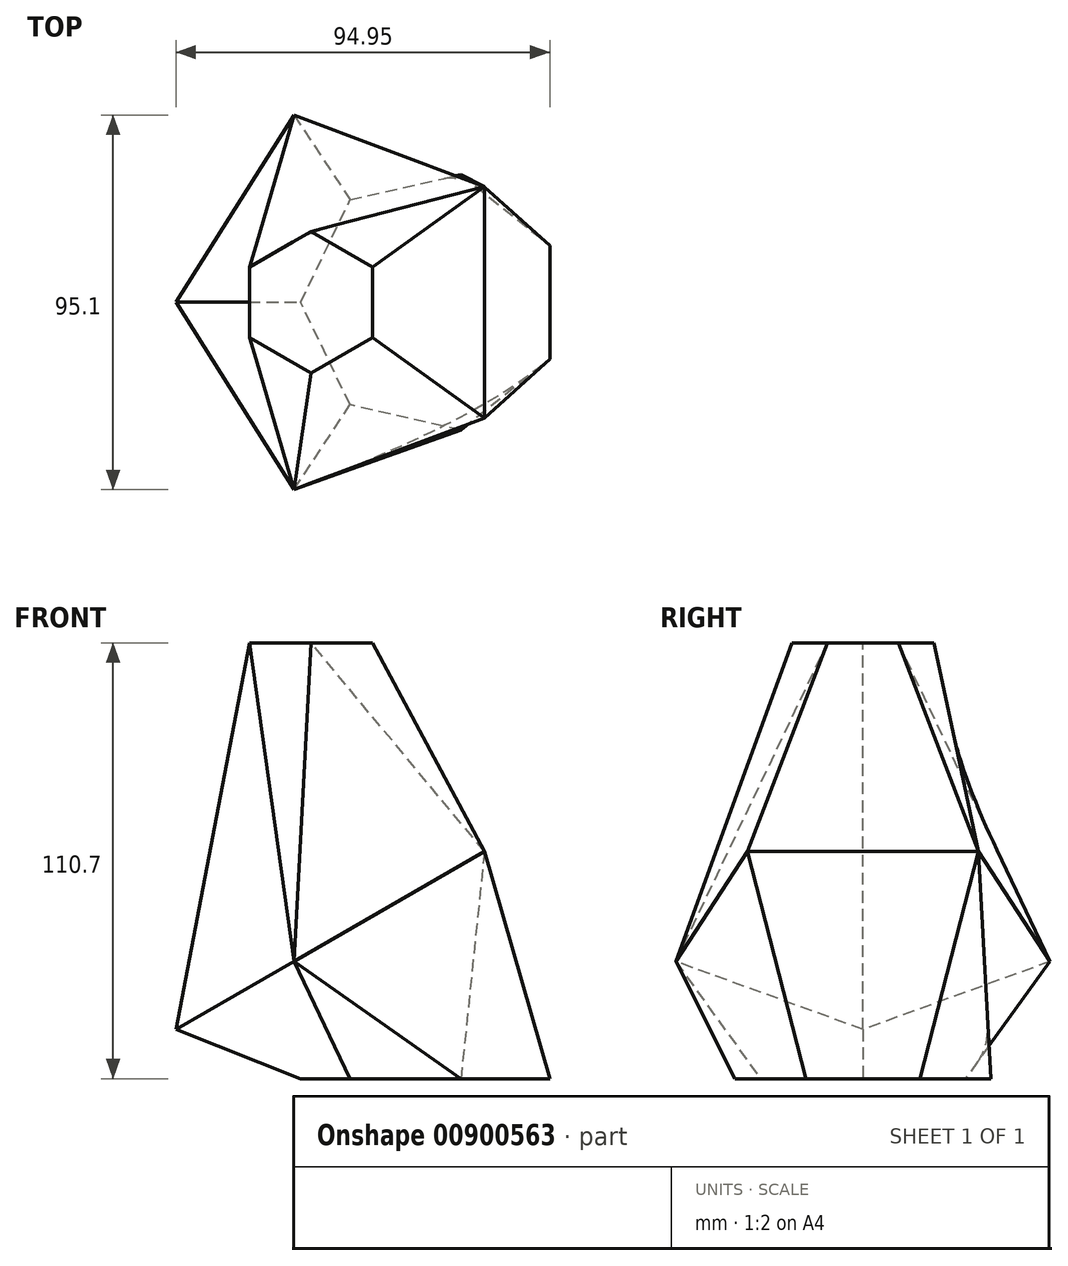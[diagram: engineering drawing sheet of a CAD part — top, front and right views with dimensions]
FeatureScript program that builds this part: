
annotation { "Feature Type Name" : "Feature", "Feature Type Description" : "" }
export const myFeature = defineFeature(function(context is Context, id is Id, definition is map)
    precondition{}
    {
        {
            var Q0;
            Q0=qCreatedBy(makeId("Top.planeOp"),FACE);
            var sketch = newSketch(context, id + "F0", { "sketchPlane" : qUnion([Q0])});
            skCircle(sketch, "E0.cCircle", {"center": v(0, 0) * mm, "radius": 30 * mm, "construction": true});
            skLineSegment(sketch, "E0.0", {"start": v(30, 14.45) * mm, "end": v(30, -14.45) * mm});
            skLineSegment(sketch, "E0.1", {"start": v(30, -14.45) * mm, "end": v(7.4, -32.46) * mm});
            skLineSegment(sketch, "E0.2", {"start": v(7.4, -32.46) * mm, "end": v(-20.76, -26.03) * mm});
            skLineSegment(sketch, "E0.3", {"start": v(-20.76, -26.03) * mm, "end": v(-33.3, 0) * mm});
            skLineSegment(sketch, "E0.4", {"start": v(-33.3, 0) * mm, "end": v(-20.76, 26.03) * mm});
            skLineSegment(sketch, "E0.5", {"start": v(-20.76, 26.03) * mm, "end": v(7.4, 32.46) * mm});
            skLineSegment(sketch, "E0.6", {"start": v(7.4, 32.46) * mm, "end": v(30, 14.45) * mm});
            skPoint(sketch, "E0.0.midPoint", {"position": v(30, 0) * mm});
            skSolve(sketch);
        }
        {
            var Q0;
            Q0=qCreatedBy(makeId("Top.planeOp"),FACE);
            cPlane(context, id + "F1", {"entities" : qUnion([Q0]), "cplaneType" : CPlaneType.OFFSET, "offset" : 50 * mm, "width" : 150 * mm, "height" : 150 * mm});
        }
        {
            var Q0;
            Q0=qCreatedBy(id+"F1.planeOp",FACE);
            var sketch = newSketch(context, id + "F2", { "sketchPlane" : qUnion([Q0])});
            skLineSegment(sketch, "E1", {"start": v(0, 42.95) * mm, "end": v(0, -21.32) * mm, "construction": true});
            skSolve(sketch);
        }
        {
            var Q0;
            Q0=sQuery(id+"F2.wireOp",EDGE,"E1");
            cPlane(context, id + "F3", {"entities" : qUnion([Q0]), "cplaneType" : CPlaneType.LINE_ANGLE, "offset" : 25 * mm, "angle" : 30 * degree, "width" : 150 * mm, "height" : 150 * mm});
        }
        {
            var Q0;
            Q0=qCreatedBy(id+"F3.planeOp",FACE);
            var sketch = newSketch(context, id + "F4", { "sketchPlane" : qUnion([Q0])});
            skCircle(sketch, "E2.cCircle", {"center": v(0, 0) * mm, "radius": 40.45 * mm, "construction": true});
            skLineSegment(sketch, "E2.0", {"start": v(40.45, 29.39) * mm, "end": v(40.45, -29.38) * mm});
            skLineSegment(sketch, "E2.1", {"start": v(40.45, -29.39) * mm, "end": v(-15.45, -47.55) * mm});
            skLineSegment(sketch, "E2.2", {"start": v(-15.45, -47.55) * mm, "end": v(-50, 0) * mm});
            skLineSegment(sketch, "E2.3", {"start": v(-50, 0) * mm, "end": v(-15.45, 47.55) * mm});
            skLineSegment(sketch, "E2.4", {"start": v(-15.45, 47.55) * mm, "end": v(-15.45, 47.55) * mm});
            skPoint(sketch, "E2.0.midPoint", {"position": v(40.45, 0) * mm});
            skLineSegment(sketch, "E3", {"start": v(-15.45, 47.55) * mm, "end": v(-15.44, 47.55) * mm});
            skLineSegment(sketch, "E4", {"start": v(-15.44, 47.55) * mm, "end": v(40.45, 29.39) * mm});
            skLineSegment(sketch, "E5", {"start": v(40.45, -29.38) * mm, "end": v(40.45, -29.39) * mm});
            skSolve(sketch);
        }
        {
            var Q0;
            Q0 = qSketchRegion(id + "F4", true);
            var Q1;
            Q1 = qSketchRegion(id + "F0", true);
            var Q2;
            Q2=sQuery(id+"F0.wireOp",VERTEX,"E0.3.end");
            var Q3;
            Q3=sQuery(id+"F4.wireOp",VERTEX,"E2.2.end");
            loft(context, id + "F5", {"startCondition" : LoftEndDerivativeType.NORMAL_TO_PROFILE, "startMagnitude" : 0, "endCondition" : LoftEndDerivativeType.NORMAL_TO_PROFILE, "endMagnitude" : 0, "sheetProfilesArray" : [{ "sheetProfileEntities" : qUnion([Q0]) }, { "sheetProfileEntities" : qUnion([Q1]) }], "matchConnections" : true, "connections" : [{ "connectionEntities" : qUnion([Q2, Q3]), "connectionEdgeQueries" : qUnion([]), "connectionEdgeParameters" : [] }]});
        }
        {
            var Q0;
            Q0=qCreatedBy(makeId("Top.planeOp"),FACE);
            var sketch = newSketch(context, id + "F6", { "sketchPlane" : qUnion([Q0])});
            skLineSegment(sketch, "E6", {"start": v(-64.74, 0) * mm, "end": v(-35, -47.87) * mm});
            skLineSegment(sketch, "E7", {"start": v(-35, -47.87) * mm, "end": v(6.83, -32.4) * mm});
            skLineSegment(sketch, "E8", {"start": v(6.83, -32.4) * mm, "end": v(13.6, -29.5) * mm});
            skLineSegment(sketch, "E9", {"start": v(13.6, -29.5) * mm, "end": v(29.8, -14.26) * mm});
            skLineSegment(sketch, "E10", {"start": v(29.8, -14.26) * mm, "end": v(29.8, 14.76) * mm});
            skLineSegment(sketch, "E11", {"start": v(29.8, 14.76) * mm, "end": v(13.36, 29.5) * mm});
            skLineSegment(sketch, "E12", {"start": v(13.36, 29.5) * mm, "end": v(7.56, 32.41) * mm});
            skLineSegment(sketch, "E13", {"start": v(5.43, 32.41) * mm, "end": v(-34.58, 47.67) * mm});
            skLineSegment(sketch, "E14", {"start": v(-34.58, 47.67) * mm, "end": v(-64.74, 0) * mm});
            skLineSegment(sketch, "E15", {"start": v(7.56, 32.41) * mm, "end": v(6.06, 32.09) * mm});
            skLineSegment(sketch, "E16", {"start": v(6.06, 32.09) * mm, "end": v(5.43, 32.41) * mm});
            skSolve(sketch);
        }
        {
            var Q0;
            Q0=makeQuery(id+"F6.imprint","IMPRINT",FACE,{"disambiguationData":[TD([[makeQuery(id+"F6.imprint","IMPRINT",EDGE,{"derivedFrom":sQuery(id+"F6.wireOp",EDGE,"E6")}),1.0]])]});
            cPlane(context, id + "F7", {"entities" : qUnion([Q0]), "cplaneType" : CPlaneType.OFFSET, "offset" : 110.7 * mm, "width" : 150 * mm, "height" : 150 * mm});
        }
        {
            var Q0;
            Q0=qCreatedBy(id+"F7.planeOp",FACE);
            var sketch = newSketch(context, id + "F8", { "sketchPlane" : qUnion([Q0])});
            skLineSegment(sketch, "E17", {"start": v(-49.6, -14.7) * mm, "end": v(-49.62, -14.7) * mm});
            skCircle(sketch, "E18.cCircle", {"center": v(-30.65, 0) * mm, "radius": 15.58 * mm, "construction": true});
            skLineSegment(sketch, "E18.0", {"start": v(-15.07, 9) * mm, "end": v(-15.07, -9) * mm});
            skLineSegment(sketch, "E18.1", {"start": v(-15.07, -9) * mm, "end": v(-30.65, -18) * mm});
            skLineSegment(sketch, "E18.2", {"start": v(-30.65, -18) * mm, "end": v(-46.24, -9) * mm});
            skLineSegment(sketch, "E18.3", {"start": v(-46.24, -9) * mm, "end": v(-46.24, 9) * mm});
            skLineSegment(sketch, "E18.4", {"start": v(-46.24, 9) * mm, "end": v(-30.65, 18) * mm});
            skLineSegment(sketch, "E18.5", {"start": v(-30.65, 18) * mm, "end": v(-15.07, 9) * mm});
            skPoint(sketch, "E18.0.midPoint", {"position": v(-15.07, 0) * mm});
            skSolve(sketch);
        }
        {
            var Q1;
            Q1=makeQuery(id+"F5.opLoft","CAP_FACE",FACE,{"disambiguationData":[OSD([makeQuery(id+"F4.imprint","IMPRINT",FACE,{"disambiguationData":[TD([[makeQuery(id+"F4.imprint","IMPRINT",EDGE,{"derivedFrom":sQuery(id+"F4.wireOp",EDGE,"E2.0")}),-1.0]])]})])],"isStart":true});
            var Q2;
            Q2 = qSketchRegion(id + "F8", true);
            loft(context, id + "F9", {"operationType" : NewBodyOperationType.ADD, "sheetProfilesArray" : [{ "sheetProfileEntities" : qUnion([Q1]) }, { "sheetProfileEntities" : qUnion([Q2]) }]});
        }
    });
